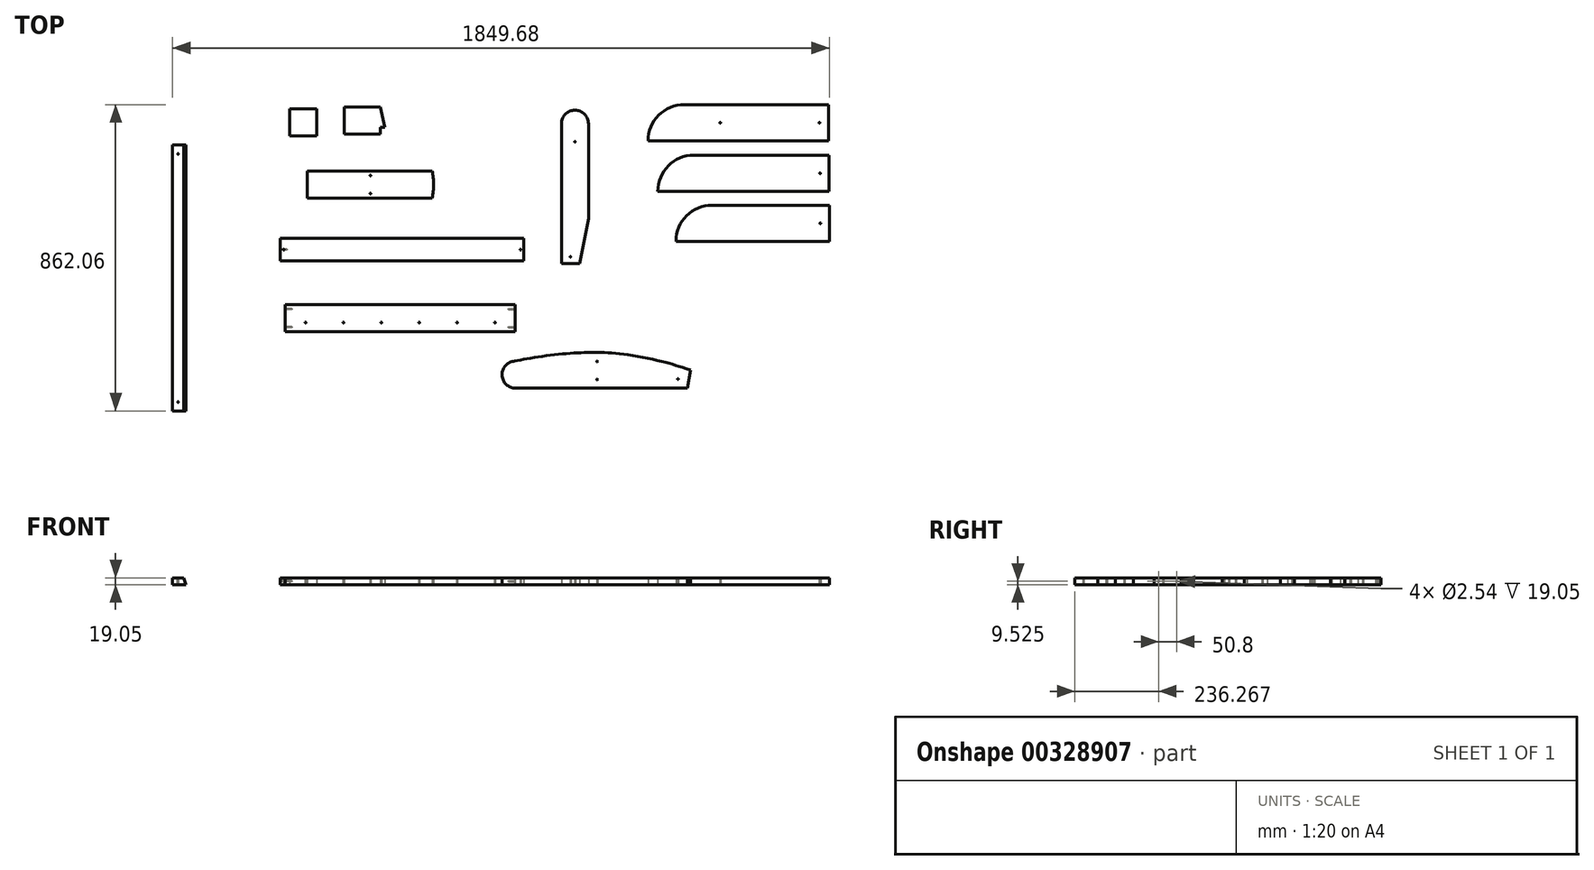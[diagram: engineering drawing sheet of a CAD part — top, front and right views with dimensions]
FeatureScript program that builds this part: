
annotation { "Feature Type Name" : "Feature", "Feature Type Description" : "" }
export const myFeature = defineFeature(function(context is Context, id is Id, definition is map)
    precondition{}
    {
        {
            var Q0;
            Q0=qCreatedBy(makeId("Top.planeOp"),FACE);
            var sketch = newSketch(context, id + "F0", { "sketchPlane" : qUnion([Q0])});
            skLineSegment(sketch, "E0", {"start": v(-60.93, -334.39) * mm, "end": v(-10.13, -334.39) * mm});
            skLineSegment(sketch, "E1", {"start": v(-10.13, -334.39) * mm, "end": v(15.27, -207.39) * mm});
            skLineSegment(sketch, "E2", {"start": v(15.27, -207.39) * mm, "end": v(15.27, 59.31) * mm});
            skLineSegment(sketch, "E3", {"start": v(-60.93, -334.39) * mm, "end": v(-60.93, 59.31) * mm});
            skLineSegment(sketch, "E4", {"start": v(-22.83, 97.41) * mm, "end": v(-22.83, 97.41) * mm});
            skPoint(sketch, "E5.visualSharp", {"position": v(-60.93, 97.41) * mm});
            skArc(sketch, "E5.filletArc", {"start": v(-22.83, 97.41) * mm, "mid": v(-49.77, 86.25) * mm, "end": v(-60.93, 59.31) * mm});
            skPoint(sketch, "E6.visualSharp", {"position": v(15.27, 97.41) * mm});
            skArc(sketch, "E6.filletArc", {"start": v(15.27, 59.31) * mm, "mid": v(4.1, 86.25) * mm, "end": v(-22.83, 97.41) * mm});
            skCircle(sketch, "E7", {"center": v(-35.53, -315.34) * mm, "radius": 1.27 * mm});
            skLineSegment(sketch, "E8", {"start": v(-22.83, 59.31) * mm, "end": v(-22.83, 8.51) * mm});
            skCircle(sketch, "E9", {"center": v(-22.83, 8.51) * mm, "radius": 1.27 * mm});
            skSolve(sketch);
        }
        {
            var Q0;
            Q0=makeQuery(id+"F0.imprint","IMPRINT",FACE,{"disambiguationData":[TD([[makeQuery(id+"F0.imprint","IMPRINT",EDGE,{"derivedFrom":sQuery(id+"F0.wireOp",EDGE,"E0")}),1.0]])]});
            extrude(context, id + "F1", {"entities" : qUnion([Q0]), "depth" : 19.05 * mm});
        }
        {
            var Q0;
            Q0=makeQuery(id+"F1.opExtrude","SWEPT_BODY",BODY,{"disambiguationData":[OSD([sQuery(id+"F0.wireOp",EDGE,"E0"),sQuery(id+"F0.wireOp",EDGE,"E1"),sQuery(id+"F0.wireOp",EDGE,"E2"),sQuery(id+"F0.wireOp",EDGE,"E3"),sQuery(id+"F0.wireOp",EDGE,"E5.filletArc"),sQuery(id+"F0.wireOp",EDGE,"E6.filletArc")])]});
            transform(context, id + "F2", {"entities" : qUnion([Q0]), "transformType" : TransformType.TRANSLATION_3D, "dx" : 812.8 * mm, "dy" : 0 * mm, "dz" : 0 * mm, "makeCopy" : true});
        }
        {
            var Q0;
            Q0=makeQuery(id+"F2.opPattern","COPY",BODY,{"derivedFrom":makeQuery(id+"F1.opExtrude","SWEPT_BODY",BODY,{"disambiguationData":[OSD([sQuery(id+"F0.wireOp",EDGE,"E0"),sQuery(id+"F0.wireOp",EDGE,"E1"),sQuery(id+"F0.wireOp",EDGE,"E2"),sQuery(id+"F0.wireOp",EDGE,"E3"),sQuery(id+"F0.wireOp",EDGE,"E5.filletArc"),sQuery(id+"F0.wireOp",EDGE,"E6.filletArc")])]}),"instanceName":"1"});
            deleteBodies(context, id + "F3", {"entities" : qUnion([Q0])});
        }
        {
            var Q0;
            Q0=qCreatedBy(makeId("Top.planeOp"),FACE);
            var sketch = newSketch(context, id + "F4", { "sketchPlane" : qUnion([Q0])});
            skLineSegment(sketch, "E10", {"start": v(261.87, -271.68) * mm, "end": v(693.67, -271.68) * mm});
            skLineSegment(sketch, "E11", {"start": v(693.67, -271.68) * mm, "end": v(693.67, -170.08) * mm});
            skLineSegment(sketch, "E12", {"start": v(693.67, -170.08) * mm, "end": v(363.47, -170.08) * mm});
            skLineSegment(sketch, "E13", {"start": v(261.87, -271.68) * mm, "end": v(261.87, -271.68) * mm});
            skPoint(sketch, "E14.visualSharp", {"position": v(261.87, -170.08) * mm});
            skArc(sketch, "E14.filletArc", {"start": v(363.47, -170.08) * mm, "mid": v(291.63, -199.84) * mm, "end": v(261.87, -271.68) * mm});
            skLineSegment(sketch, "E15", {"start": v(693.67, -220.88) * mm, "end": v(668.27, -220.88) * mm});
            skCircle(sketch, "E16", {"center": v(668.27, -220.88) * mm, "radius": 1.27 * mm});
            skSolve(sketch);
        }
        {
            var Q0;
            Q0 = qSketchRegion(id + "F4", true);
            extrude(context, id + "F5", {"entities" : qUnion([Q0]), "depth" : 19.05 * mm});
        }
        {
            var Q0;
            Q0=qCreatedBy(makeId("Top.planeOp"),FACE);
            var sketch = newSketch(context, id + "F6", { "sketchPlane" : qUnion([Q0])});
            skLineSegment(sketch, "E17", {"start": v(693.1, -131) * mm, "end": v(210.5, -131) * mm});
            skLineSegment(sketch, "E18", {"start": v(210.5, -131) * mm, "end": v(210.5, -131) * mm});
            skLineSegment(sketch, "E19", {"start": v(312.1, -29.4) * mm, "end": v(693.1, -29.4) * mm});
            skLineSegment(sketch, "E20", {"start": v(693.1, -29.4) * mm, "end": v(693.1, -131) * mm});
            skPoint(sketch, "E21.visualSharp", {"position": v(210.5, -29.4) * mm});
            skArc(sketch, "E21.filletArc", {"start": v(312.1, -29.4) * mm, "mid": v(240.26, -59.17) * mm, "end": v(210.5, -131) * mm});
            skLineSegment(sketch, "E22", {"start": v(693.1, -80.2) * mm, "end": v(667.7, -80.2) * mm});
            skCircle(sketch, "E23", {"center": v(667.7, -80.2) * mm, "radius": 1.27 * mm});
            skSolve(sketch);
        }
        {
            var Q0;
            Q0=makeQuery(id+"F6.imprint","IMPRINT",FACE,{"disambiguationData":[TD([[makeQuery(id+"F6.imprint","IMPRINT",EDGE,{"derivedFrom":sQuery(id+"F6.wireOp",EDGE,"E17")}),-1.0]])]});
            extrude(context, id + "F7", {"entities" : qUnion([Q0]), "depth" : 19.05 * mm});
        }
        {
            var Q0;
            Q0=qCreatedBy(makeId("Top.planeOp"),FACE);
            var sketch = newSketch(context, id + "F8", { "sketchPlane" : qUnion([Q0])});
            skLineSegment(sketch, "E24", {"start": v(691.12, 11.16) * mm, "end": v(691.12, 112.76) * mm});
            skLineSegment(sketch, "E25", {"start": v(691.12, 112.76) * mm, "end": v(284.72, 112.76) * mm});
            skLineSegment(sketch, "E26", {"start": v(183.12, 11.16) * mm, "end": v(183.12, 11.16) * mm});
            skLineSegment(sketch, "E27", {"start": v(183.12, 11.16) * mm, "end": v(691.12, 11.16) * mm});
            skPoint(sketch, "E28.visualSharp", {"position": v(183.12, 112.76) * mm});
            skArc(sketch, "E28.filletArc", {"start": v(284.72, 112.76) * mm, "mid": v(212.88, 83) * mm, "end": v(183.12, 11.16) * mm});
            skLineSegment(sketch, "E29", {"start": v(691.12, 61.96) * mm, "end": v(665.72, 61.96) * mm});
            skPoint(sketch, "E29.endSnap0", {"position": v(691.12, 61.96) * mm});
            skCircle(sketch, "E30", {"center": v(665.72, 61.96) * mm, "radius": 1.27 * mm});
            skCircle(sketch, "E31", {"center": v(386.32, 61.96) * mm, "radius": 1.27 * mm});
            skSolve(sketch);
        }
        {
            var Q0;
            Q0 = qSketchRegion(id + "F8", true);
            extrude(context, id + "F9", {"entities" : qUnion([Q0]), "depth" : 19.05 * mm});
        }
        {
            var Q0;
            Q0=qCreatedBy(makeId("Top.planeOp"),FACE);
            var sketch = newSketch(context, id + "F10", { "sketchPlane" : qUnion([Q0])});
            skLineSegment(sketch, "E32", {"start": v(-189.76, -685.16) * mm, "end": v(293.53, -685.16) * mm});
            skPoint(sketch, "E33.visualSharp", {"position": v(-227.17, -685.16) * mm});
            skLineSegment(sketch, "E34", {"start": v(302.65, -634.36) * mm, "end": v(293.53, -685.16) * mm});
            skArc(sketch, "E35", {"start": v(-192.66, -609.06) * mm, "mid": v(-228.06, -648.51) * mm, "end": v(-189.76, -685.16) * mm});
            skLineSegment(sketch, "E36", {"start": v(39.53, -686.26) * mm, "end": v(39.53, -584.66) * mm});
            skFitSpline(sketch, "E37", {"points": [v(302.87, -634.43) * mm, v(233.44, -612.87) * mm, v(116.11, -589.95) * mm, v(39.53, -584.66) * mm, v(-71.82, -590.25) * mm, v(-192.66, -609.06) * mm], "startDerivative": vector(-538.27, 166.6) * mm, "endDerivative": vector(-386.07, -76.56) * mm});
            skLineSegment(sketch, "E38", {"start": v(39.53, -686.26) * mm, "end": v(39.53, -660.86) * mm});
            skLineSegment(sketch, "E39", {"start": v(39.53, -584.66) * mm, "end": v(39.53, -610.06) * mm});
            skCircle(sketch, "E40", {"center": v(39.53, -610.06) * mm, "radius": 1.27 * mm});
            skCircle(sketch, "E41", {"center": v(39.53, -660.86) * mm, "radius": 1.27 * mm});
            skCircle(sketch, "E42", {"center": v(267.44, -659.76) * mm, "radius": 1.27 * mm});
            skSolve(sketch);
        }
        {
            var Q0;
            {var subQ0=sQuery(id+"F10.wireOp",EDGE,"E35");Q0=makeQuery(id+"F10.imprint","IMPRINT",FACE,{"disambiguationData":[TD([[makeQuery(id+"F10.imprint","IMPRINT",EDGE,{"derivedFrom":subQ0}),1.0]])]});}
            var Q1;
            {var subQ0=sQuery(id+"F10.wireOp",EDGE,"E34");Q1=makeQuery(id+"F10.imprint","IMPRINT",FACE,{"disambiguationData":[TD([[makeQuery(id+"F10.imprint","IMPRINT",EDGE,{"derivedFrom":subQ0}),-1.0]])]});}
            extrude(context, id + "F11", {"entities" : qUnion([Q0, Q1]), "depth" : 19.05 * mm});
        }
        {
            var Q0;
            Q0=qCreatedBy(makeId("Top.planeOp"),FACE);
            var sketch = newSketch(context, id + "F12", { "sketchPlane" : qUnion([Q0])});
            skLineSegment(sketch, "E43", {"start": v(-838.56, -525.73) * mm, "end": v(-190.86, -525.73) * mm});
            skLineSegment(sketch, "E44", {"start": v(-190.86, -525.73) * mm, "end": v(-190.86, -449.53) * mm});
            skLineSegment(sketch, "E45", {"start": v(-838.56, -525.73) * mm, "end": v(-838.56, -449.53) * mm});
            skLineSegment(sketch, "E46", {"start": v(-838.56, -449.53) * mm, "end": v(-190.86, -449.53) * mm});
            skLineSegment(sketch, "E47", {"start": v(-838.56, -525.73) * mm, "end": v(-838.56, -500.33) * mm});
            skCircle(sketch, "E48", {"center": v(-781.41, -500.33) * mm, "radius": 1.27 * mm});
            skCircle(sketch, "E49", {"center": v(-674.73, -500.33) * mm, "radius": 1.27 * mm});
            skCircle(sketch, "E50", {"center": v(-568.05, -500.33) * mm, "radius": 1.27 * mm});
            skCircle(sketch, "E51.MirrorC", {"center": v(-461.37, -500.33) * mm, "radius": 1.27 * mm});
            skCircle(sketch, "E52.MirrorC", {"center": v(-248.01, -500.33) * mm, "radius": 1.27 * mm});
            skCircle(sketch, "E53.MirrorC", {"center": v(-354.7, -500.33) * mm, "radius": 1.27 * mm});
            skSolve(sketch);
        }
        {
            var Q0;
            Q0=makeQuery(id+"F12.imprint","IMPRINT",FACE,{"disambiguationData":[TD([[makeQuery(id+"F12.imprint","IMPRINT",EDGE,{"derivedFrom":sQuery(id+"F12.wireOp",EDGE,"E43")}),1.0]])]});
            extrude(context, id + "F13", {"entities" : qUnion([Q0]), "depth" : 19.05 * mm});
        }
        {
            var Q0;
            Q0=qCreatedBy(makeId("Front.planeOp"),FACE);
            var sketch = newSketch(context, id + "F14", { "sketchPlane" : qUnion([Q0])});
            skLineSegment(sketch, "E54", {"start": v(-1156, 0) * mm, "end": v(-1156, 19.05) * mm});
            skLineSegment(sketch, "E55", {"start": v(-1156, 0) * mm, "end": v(-1117.9, 0) * mm});
            skLineSegment(sketch, "E56", {"start": v(-1117.9, 0) * mm, "end": v(-1125, 19.05) * mm});
            skLineSegment(sketch, "E57", {"start": v(-1125, 19.05) * mm, "end": v(-1156, 19.05) * mm});
            skSolve(sketch);
        }
        {
            var Q0;
            Q0=makeQuery(id+"F14.imprint","IMPRINT",FACE,{"disambiguationData":[TD([[makeQuery(id+"F14.imprint","IMPRINT",EDGE,{"derivedFrom":sQuery(id+"F14.wireOp",EDGE,"E54")}),-1.0]])]});
            extrude(context, id + "F15", {"entities" : qUnion([Q0]), "depth" : 749.3 * mm});
        }
        {
            var Q0;
            Q0=qCreatedBy(makeId("Top.planeOp"),FACE);
            var sketch = newSketch(context, id + "F16", { "sketchPlane" : qUnion([Q0])});
            skLineSegment(sketch, "E58", {"start": v(-852.78, -327.36) * mm, "end": v(-166.98, -327.36) * mm});
            skLineSegment(sketch, "E59", {"start": v(-166.98, -327.36) * mm, "end": v(-166.98, -263.86) * mm});
            skLineSegment(sketch, "E60", {"start": v(-166.98, -263.86) * mm, "end": v(-852.78, -263.86) * mm});
            skLineSegment(sketch, "E61", {"start": v(-852.78, -263.86) * mm, "end": v(-852.78, -327.36) * mm});
            skCircle(sketch, "E62", {"center": v(-843, -295.61) * mm, "radius": 1.27 * mm});
            skPoint(sketch, "E62.centerSnap0", {"position": v(-852.78, -295.61) * mm});
            skLineSegment(sketch, "E63", {"start": v(-166.98, -295.61) * mm, "end": v(-176.26, -295.61) * mm});
            skCircle(sketch, "E64", {"center": v(-176.26, -295.61) * mm, "radius": 1.27 * mm});
            skSolve(sketch);
        }
        {
            var Q0;
            Q0=makeQuery(id+"F16.imprint","IMPRINT",FACE,{"disambiguationData":[TD([[makeQuery(id+"F16.imprint","IMPRINT",EDGE,{"derivedFrom":sQuery(id+"F16.wireOp",EDGE,"E58")}),1.0]])]});
            extrude(context, id + "F17", {"entities" : qUnion([Q0]), "depth" : 19.05 * mm});
        }
        {
            var Q0;
            Q0=qCreatedBy(makeId("Top.planeOp"),FACE);
            var sketch = newSketch(context, id + "F18", { "sketchPlane" : qUnion([Q0])});
            skLineSegment(sketch, "E65", {"start": v(-776.42, -73.8) * mm, "end": v(-776.42, -150) * mm});
            skLineSegment(sketch, "E66", {"start": v(-776.42, -150) * mm, "end": v(-424.95, -150) * mm});
            skLineSegment(sketch, "E67", {"start": v(-424.95, -73.8) * mm, "end": v(-776.42, -73.8) * mm});
            skLineSegment(sketch, "E68", {"start": v(-598.62, -150) * mm, "end": v(-598.62, -137.3) * mm});
            skPoint(sketch, "E69.endSnap0", {"position": v(-598.62, -73.8) * mm});
            skCircle(sketch, "E70", {"center": v(-598.62, -86.5) * mm, "radius": 1.27 * mm});
            skCircle(sketch, "E71", {"center": v(-598.62, -137.3) * mm, "radius": 1.27 * mm});
            skPoint(sketch, "E72.centerSnap0", {"position": v(-776.42, -111.9) * mm});
            skArc(sketch, "E73.trimOffspring", {"start": v(-424.95, -150) * mm, "mid": v(-420.82, -111.9) * mm, "end": v(-424.95, -73.8) * mm});
            skPoint(sketch, "E74.orphan", {"position": v(-420.82, -73.8) * mm});
            skPoint(sketch, "E75.orphan", {"position": v(-420.82, -150) * mm});
            skSolve(sketch);
        }
        {
            var Q0;
            Q0=makeQuery(id+"F18.imprint","IMPRINT",FACE,{"disambiguationData":[TD([[makeQuery(id+"F18.imprint","IMPRINT",EDGE,{"derivedFrom":sQuery(id+"F18.wireOp",EDGE,"E65")}),1.0]])]});
            extrude(context, id + "F19", {"entities" : qUnion([Q0]), "depth" : 19.05 * mm});
        }
        {
            var Q0;
            Q0=qCreatedBy(makeId("Top.planeOp"),FACE);
            var sketch = newSketch(context, id + "F20", { "sketchPlane" : qUnion([Q0])});
            skLineSegment(sketch, "E76", {"start": v(-750.24, 101.28) * mm, "end": v(-750.24, 25.08) * mm});
            skLineSegment(sketch, "E77", {"start": v(-750.24, 25.08) * mm, "end": v(-826.44, 25.08) * mm});
            skLineSegment(sketch, "E78", {"start": v(-826.44, 25.08) * mm, "end": v(-826.44, 101.28) * mm});
            skLineSegment(sketch, "E79", {"start": v(-826.44, 101.28) * mm, "end": v(-750.24, 101.28) * mm});
            skSolve(sketch);
        }
        {
            var Q0;
            Q0=makeQuery(id+"F20.imprint","IMPRINT",FACE,{"disambiguationData":[TD([[makeQuery(id+"F20.imprint","IMPRINT",EDGE,{"derivedFrom":sQuery(id+"F20.wireOp",EDGE,"E76")}),-1.0]])]});
            extrude(context, id + "F21", {"entities" : qUnion([Q0]), "depth" : 19.05 * mm});
        }
        {
            var Q0;
            Q0=qCreatedBy(makeId("Top.planeOp"),FACE);
            var sketch = newSketch(context, id + "F22", { "sketchPlane" : qUnion([Q0])});
            skLineSegment(sketch, "E80", {"start": v(-671.98, 105.83) * mm, "end": v(-671.98, 29.63) * mm});
            skLineSegment(sketch, "E81", {"start": v(-671.98, 29.63) * mm, "end": v(-570.38, 29.63) * mm});
            skLineSegment(sketch, "E82", {"start": v(-570.38, 105.83) * mm, "end": v(-671.98, 105.83) * mm});
            skLineSegment(sketch, "E83", {"start": v(-570.38, 29.63) * mm, "end": v(-570.38, 48.68) * mm});
            skLineSegment(sketch, "E84", {"start": v(-570.38, 48.68) * mm, "end": v(-557.68, 48.68) * mm});
            skLineSegment(sketch, "E85", {"start": v(-557.68, 48.68) * mm, "end": v(-570.38, 105.83) * mm});
            skSolve(sketch);
        }
        {
            var Q0;
            Q0=makeQuery(id+"F22.imprint","IMPRINT",FACE,{"disambiguationData":[TD([[makeQuery(id+"F22.imprint","IMPRINT",EDGE,{"derivedFrom":sQuery(id+"F22.wireOp",EDGE,"E80")}),1.0]])]});
            extrude(context, id + "F23", {"entities" : qUnion([Q0]), "depth" : 19.05 * mm});
        }
        {
            var Q0;
            Q0=sQuery(id+"F0.wireOp",EDGE,"E7");
            extrude(context, id + "F24", {"bodyType" : ToolBodyType.SURFACE, "surfaceEntities" : qUnion([Q0]), "depth" : 19.05 * mm});
        }
        {
            var Q0;
            Q0=sQuery(id+"F0.wireOp",EDGE,"E9");
            extrude(context, id + "F25", {"bodyType" : ToolBodyType.SURFACE, "surfaceEntities" : qUnion([Q0]), "depth" : 25.4 * mm});
        }
        {
            var Q0;
            Q0=sQuery(id+"F10.wireOp",EDGE,"E40");
            extrude(context, id + "F26", {"bodyType" : ToolBodyType.SURFACE, "surfaceEntities" : qUnion([Q0]), "depth" : 25.4 * mm});
        }
        {
            var Q0;
            Q0=makeQuery(id+"F15.opExtrude","SWEPT_FACE",FACE,{"disambiguationData":[OSD([sQuery(id+"F14.wireOp",EDGE,"E57")])]});
            var sketch = newSketch(context, id + "F27", { "sketchPlane" : qUnion([Q0])});
            skLineSegment(sketch, "E86", {"start": v(-1140.5, -749.3) * mm, "end": v(-1140.5, -723.9) * mm});
            skCircle(sketch, "E87", {"center": v(-1140.5, -723.9) * mm, "radius": 1.27 * mm});
            skLineSegment(sketch, "E88", {"start": v(-1140.5, 0) * mm, "end": v(-1140.5, -25.4) * mm});
            skCircle(sketch, "E89", {"center": v(-1140.5, -25.4) * mm, "radius": 1.27 * mm});
            skSolve(sketch);
        }
        {
            var Q0;
            Q0 = qSketchRegion(id + "F27", true);
            extrude(context, id + "F28", {"entities" : qUnion([Q0]), "operationType" : NewBodyOperationType.REMOVE, "depth" : -19.05 * mm});
        }
        {
            var Q0;
            Q0=makeQuery(id+"F13.opExtrude","SWEPT_FACE",FACE,{"disambiguationData":[OSD([sQuery(id+"F12.wireOp",EDGE,"E45"),sQuery(id+"F12.wireOp",EDGE,"E47")])]});
            var sketch = newSketch(context, id + "F29", { "sketchPlane" : qUnion([Q0])});
            skLineSegment(sketch, "E90", {"start": v(525.73, 9.53) * mm, "end": v(513.03, 9.53) * mm});
            skCircle(sketch, "E91", {"center": v(462.23, 9.53) * mm, "radius": 1.27 * mm});
            skCircle(sketch, "E92", {"center": v(513.03, 9.53) * mm, "radius": 1.27 * mm});
            skSolve(sketch);
        }
        {
            var Q0;
            Q0 = qSketchRegion(id + "F29", true);
            extrude(context, id + "F30", {"entities" : qUnion([Q0]), "operationType" : NewBodyOperationType.REMOVE, "oppositeDirection" : true, "depth" : 19.05 * mm});
        }
        {
            var Q0;
            Q0=makeQuery(id+"F13.opExtrude","SWEPT_FACE",FACE,{"disambiguationData":[OSD([sQuery(id+"F12.wireOp",EDGE,"E44")])]});
            var sketch = newSketch(context, id + "F31", { "sketchPlane" : qUnion([Q0])});
            skLineSegment(sketch, "E93", {"start": v(-525.73, 9.53) * mm, "end": v(-513.03, 9.53) * mm});
            skCircle(sketch, "E94", {"center": v(-462.23, 9.53) * mm, "radius": 1.27 * mm});
            skCircle(sketch, "E95", {"center": v(-513.03, 9.53) * mm, "radius": 1.27 * mm});
            skSolve(sketch);
        }
        {
            var Q0;
            Q0 = qSketchRegion(id + "F31", true);
            extrude(context, id + "F32", {"entities" : qUnion([Q0]), "operationType" : NewBodyOperationType.REMOVE, "oppositeDirection" : true, "depth" : 19.05 * mm});
        }
        {
            var Q0;
            Q0=makeQuery(id+"F17.opExtrude","SWEPT_FACE",FACE,{"disambiguationData":[OSD([sQuery(id+"F16.wireOp",EDGE,"E61")])]});
            var sketch = newSketch(context, id + "F33", { "sketchPlane" : qUnion([Q0])});
            skCircle(sketch, "E96", {"center": v(295.61, 9.53) * mm, "radius": 1.27 * mm});
            skPoint(sketch, "E96.centerSnap0", {"position": v(295.61, 19.05) * mm});
            skPoint(sketch, "E96.centerSnap1", {"position": v(263.86, 9.53) * mm});
            skSolve(sketch);
        }
        {
            var Q0;
            Q0 = qSketchRegion(id + "F33", true);
            extrude(context, id + "F34", {"entities" : qUnion([Q0]), "operationType" : NewBodyOperationType.REMOVE, "oppositeDirection" : true, "depth" : 19.05 * mm});
        }
    });
